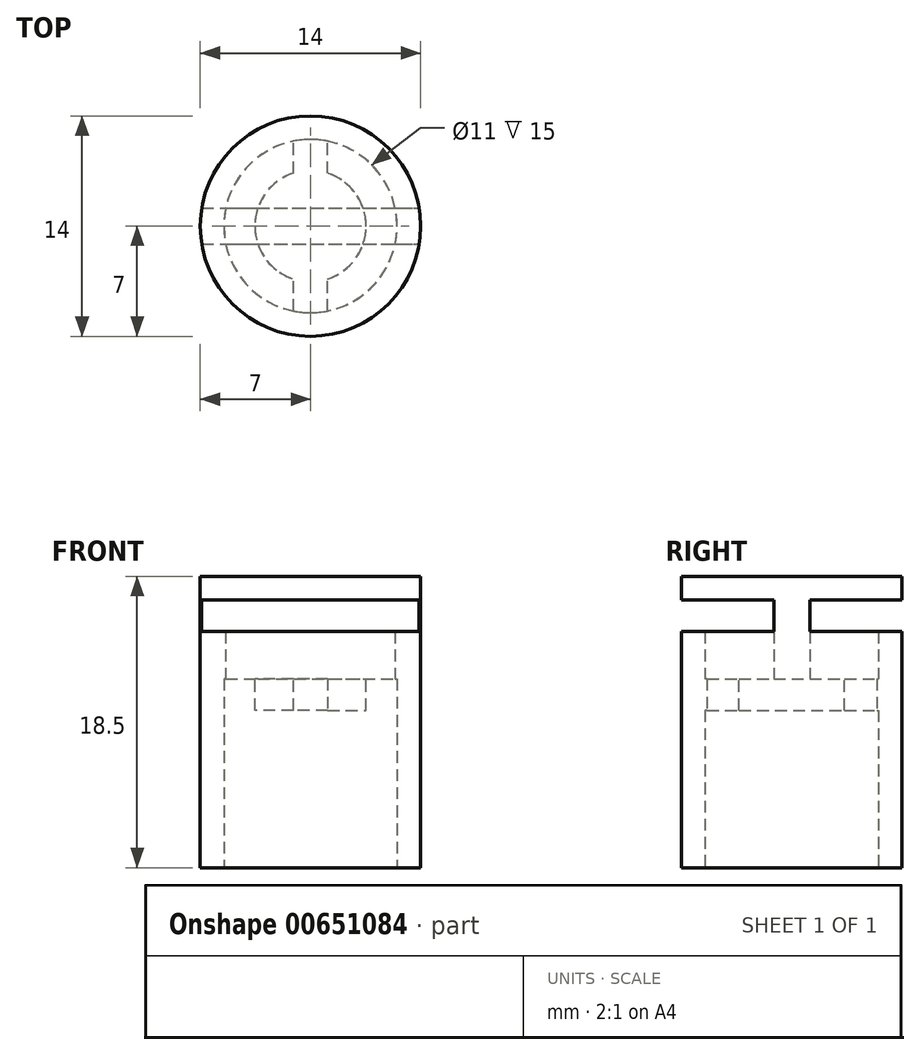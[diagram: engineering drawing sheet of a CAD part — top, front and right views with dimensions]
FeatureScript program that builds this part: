
annotation { "Feature Type Name" : "Feature", "Feature Type Description" : "" }
export const myFeature = defineFeature(function(context is Context, id is Id, definition is map)
    precondition{}
    {
        {
            var Q0;
            Q0=qCreatedBy(makeId("Top.planeOp"),FACE);
            var sketch = newSketch(context, id + "F0", { "sketchPlane" : qUnion([Q0])});
            skCircle(sketch, "E0", {"center": v(0, 0) * mm, "radius": 7 * mm});
            skSolve(sketch);
        }
        {
            var Q0;
            Q0=qSketchRegion(id+"F0",true);
            extrude(context, id + "F1", {"entities" : qUnion([Q0]), "depth" : 15 * mm, "offsetDistance" : 25 * mm});
        }
        {
            var Q0;
            Q0=makeQuery(id+"F1.opExtrude","CAP_FACE",FACE,{"disambiguationData":[OSD([sQuery(id+"F0.wireOp",EDGE,"E0")])],"isStart":true});
            var sketch = newSketch(context, id + "F2", { "sketchPlane" : qUnion([Q0])});
            skCircle(sketch, "E1.0", {"center": v(0, 0) * mm, "radius": 5.5 * mm});
            skSolve(sketch);
        }
        {
            var Q0;
            Q0=qSketchRegion(id+"F2",true);
            extrude(context, id + "F3", {"entities" : qUnion([Q0]), "operationType" : NewBodyOperationType.REMOVE, "endBound" : BoundingType.THROUGH_ALL, "oppositeDirection" : true, "depth" : 8 * mm, "offsetDistance" : 25 * mm});
        }
        {
            var Q0;
            Q0=makeQuery(id+"F1.opExtrude","CAP_FACE",FACE,{"disambiguationData":[OSD([sQuery(id+"F0.wireOp",EDGE,"E0")])],"isStart":false});
            cPlane(context, id + "F4", {"entities" : qUnion([Q0]), "cplaneType" : CPlaneType.OFFSET, "offset" : 2 * mm, "width" : 150 * mm, "height" : 150 * mm});
        }
        {
            var Q0;
            Q0=qCreatedBy(id+"F4.planeOp",FACE);
            var sketch = newSketch(context, id + "F5", { "sketchPlane" : qUnion([Q0])});
            skCircle(sketch, "E2", {"center": v(0, 0) * mm, "radius": 7 * mm});
            skSolve(sketch);
        }
        {
            var Q0;
            Q0 = qSketchRegion(id + "F5", true);
            extrude(context, id + "F6", {"entities" : qUnion([Q0]), "depth" : 1.5 * mm, "offsetDistance" : 25 * mm});
        }
        {
            var Q0;
            Q0=makeQuery(id+"F6.opExtrude","CAP_FACE",FACE,{"disambiguationData":[OSD([sQuery(id+"F5.wireOp",EDGE,"E2")])],"isStart":true});
            var sketch = newSketch(context, id + "F7", { "sketchPlane" : qUnion([Q0])});
            skLineSegment(sketch, "E3.bottom", {"start": v(-6.9, 1.15) * mm, "end": v(6.9, 1.15) * mm});
            skLineSegment(sketch, "E3.top", {"start": v(-6.9, -1.15) * mm, "end": v(6.9, -1.15) * mm});
            skPoint(sketch, "E3.middle", {"position": v(0, 0) * mm});
            skArc(sketch, "E4.0", {"start": v(-6.9, 1.15) * mm, "mid": v(-7, 0) * mm, "end": v(-6.9, -1.15) * mm});
            skArc(sketch, "E5.trimOffspring", {"start": v(6.9, -1.15) * mm, "mid": v(7, 0) * mm, "end": v(6.9, 1.15) * mm});
            skPoint(sketch, "E3.right.end.orphan", {"position": v(8.1, -1.15) * mm});
            skPoint(sketch, "E3.right.start.orphan", {"position": v(8.1, 1.15) * mm});
            skPoint(sketch, "E3.left.end.orphan", {"position": v(-8.1, -1.15) * mm});
            skPoint(sketch, "E3.left.start.orphan", {"position": v(-8.1, 1.15) * mm});
            skSolve(sketch);
        }
        {
            var Q0;
            Q0 = qSketchRegion(id + "F7", true);
            extrude(context, id + "F8", {"entities" : qUnion([Q0]), "operationType" : NewBodyOperationType.ADD, "depth" : 5 * mm, "offsetDistance" : 25 * mm});
        }
        {
            var Q0;
            Q0=makeQuery(id+"F8.opExtrude","CAP_FACE",FACE,{"disambiguationData":[OSD([sQuery(id+"F7.wireOp",EDGE,"E3.bottom"),sQuery(id+"F7.wireOp",EDGE,"E3.top"),sQuery(id+"F7.wireOp",EDGE,"E4.0"),sQuery(id+"F7.wireOp",EDGE,"E5.trimOffspring")])],"isStart":false});
            var sketch = newSketch(context, id + "F9", { "sketchPlane" : qUnion([Q0])});
            skCircle(sketch, "E6", {"center": v(0, 0) * mm, "radius": 3.53 * mm});
            skSolve(sketch);
        }
        {
            var Q0;
            Q0 = qSketchRegion(id + "F9", true);
            var Q1;
            Q1=sQuery(id+"F9.wireOp",EDGE,"E6");
            extrude(context, id + "F10", {"entities" : qUnion([Q0]), "operationType" : NewBodyOperationType.ADD, "surfaceEntities" : qUnion([Q1]), "depth" : 2 * mm, "offsetDistance" : 25 * mm});
        }
        {
            var Q0;
            Q0=makeQuery(id+"F10.boolean.opBoolean","SPLIT",FACE,{"disambiguationData":[OD(0.0)],"derivedFrom":makeQuery(id+"F8.opExtrude","CAP_FACE",FACE,{"disambiguationData":[OSD([sQuery(id+"F7.wireOp",EDGE,"E3.bottom"),sQuery(id+"F7.wireOp",EDGE,"E3.top"),sQuery(id+"F7.wireOp",EDGE,"E4.0"),sQuery(id+"F7.wireOp",EDGE,"E5.trimOffspring")])],"isStart":false})});
            var sketch = newSketch(context, id + "F11", { "sketchPlane" : qUnion([Q0])});
            skLineSegment(sketch, "E7.bottom", {"start": v(-1.1, 6.03) * mm, "end": v(1.1, 6.03) * mm});
            skLineSegment(sketch, "E7.top", {"start": v(-1.1, -6.03) * mm, "end": v(1.1, -6.03) * mm});
            skLineSegment(sketch, "E7.left", {"start": v(-1.1, 6.03) * mm, "end": v(-1.1, -6.03) * mm});
            skLineSegment(sketch, "E7.right", {"start": v(1.1, 6.03) * mm, "end": v(1.1, -6.03) * mm});
            skPoint(sketch, "E7.middle", {"position": v(0, 0) * mm});
            skSolve(sketch);
        }
        {
            var Q0;
            Q0 = qSketchRegion(id + "F11", true);
            var Q1;
            Q1=sQuery(id+"F11.wireOp",EDGE,"E7.left");
            extrude(context, id + "F12", {"entities" : qUnion([Q0]), "operationType" : NewBodyOperationType.ADD, "surfaceEntities" : qUnion([Q1]), "depth" : 2 * mm, "offsetDistance" : 25 * mm});
        }
    });
